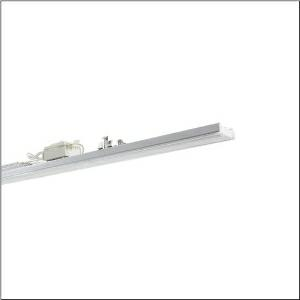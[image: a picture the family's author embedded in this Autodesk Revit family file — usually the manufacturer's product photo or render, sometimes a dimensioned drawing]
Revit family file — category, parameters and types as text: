
# Revit family: licross_r__11_recessed_mo_51tl12dn4axg3c_2e33
name_source: partatom
category: Lighting Fixtures
units: mm (PartAtom-declared; Revit-internal decimal feet)

## family parameters
Cut with Voids When Loaded = No
Host = Face
Light Source = No
Part Type = Normal
Room Calculation Point = No
Round Connector Dimension = Use Diameter
Shared = No

## types (1)
- --- (1 x LED, 1010 lm, 6.7 W, 4000K)
    Apparent Load = 7 VA
    CIE Flux Codes = 67 92 99 100 100
    Color Rendering = 80
    Color Temperature = 4000K
    Default Elevation = 1800 mm
    Description = Licross® 11 Recessed MO, luminaire insert, of sheet steel, coil coated, white, length: 1.500mm, width: 66mm, height: 67mm, LED rated luminous flux: 10.240lm, light colour: 840, control gear: DALI 2 (for two DALI lines), with plug, 6-pole, with phase selection, for trunking rail, 14-core, mains connection: 220..240V, AC, 50/60Hz, rated input power: 61W, for trunking rail, 14-core, halogen-free wiring, for emergency light function, converter,control gear: single battery element, battery: LiFePO4, 9Ah, primary optical cover: cover, of PMMA, light emission: direct distribution, primary light characteristic: symmetric, protection rating (complete): IP40, insulation class (complete): insulation class I (protective earthing), certification: CE, UKCA, protection symbol: D if used in an environment without relevant dust loads with corresponding accessories, impact resistance: IK06, permissible ambient temperature for indoor applications: +5..+35°C, standard: EN 60598-2-22, LABS conformity tested according to VDMA 24364:2018-05, reducing of maximum allowable ambient temperature of 5°C with ceiling mounting, corresponds to IFS (International Featured Standards) requirements for safety and quality in the food industry, packaging unit: 1 piece
    Height = 58 mm
    Lamp = 1 x LED
    Lamp Light Flux = 1010 lm
    Lamp Power = 6.7 W
    Lamp count = 1
    Length = 1500 mm
    Luminous efficacy = 151 lm/W
    Manufacturer = Siteco
    ModVariant = No
    Model = 51TL12DN4AXG3C
    Mounting Place = Ceiling
    Mounting Type = Pendant
    Number of Poles = 1
    OnlyDefault = Yes
    Power Factor = 1
    Product Name = Licross® 11 Recessed MO
    Product group = luminaire insert
    ProductGroupID = 902
    Protection Class = Protection class I
    Protection Degree = IP 40
    RLX_Detail_Level = 1
    RLX_Emergency_Light_Flux = 0 lm
    RLX_Emergency_Type = 0
    RLX_Emergency_Type_DB = No
    RlxData = <blob elided: 24745 chars, md5=5569c92e>
    Socket = socket
    Standby Power = 0 W
    System Light Flux = 1010 lm
    System Power = 7 W
    Type Comments = : emergency light operation: 3 h
    Type Image = l_1296930.jpg
    URL = http://relux.com
    VarID = @adj_090178
    Voltage = 0 V
    Weight = 0.00 kg
    Width = 66 mm

## geometry (parser evidence)
native form markers: Blend x4, Sweep x9
no freeform markers — native parametric forms only
